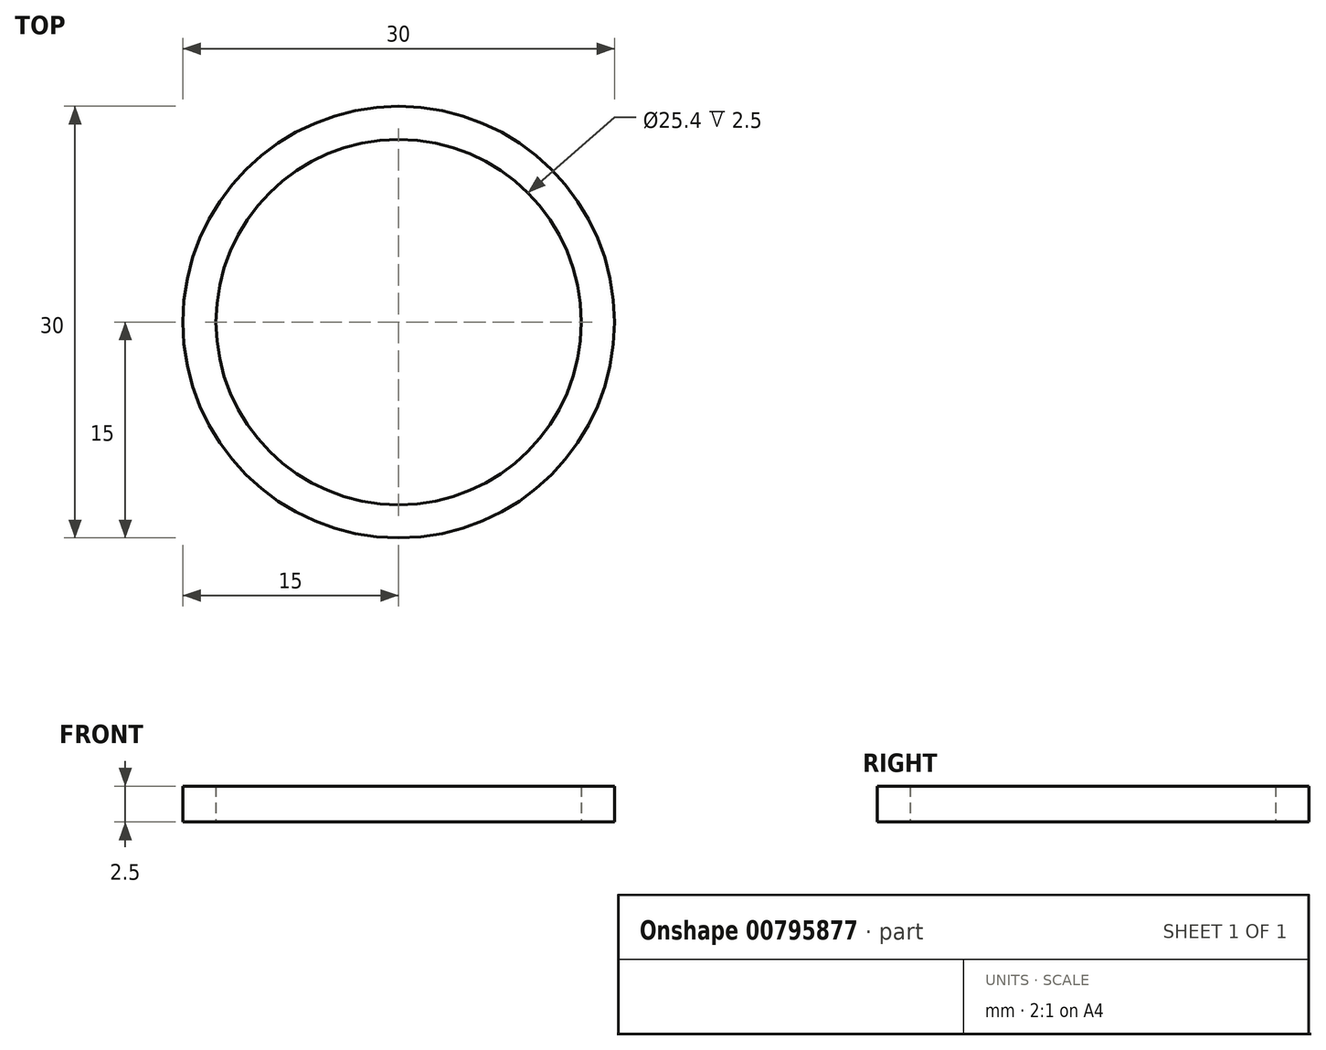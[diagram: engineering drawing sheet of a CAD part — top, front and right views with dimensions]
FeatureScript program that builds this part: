
annotation { "Feature Type Name" : "Feature", "Feature Type Description" : "" }
export const myFeature = defineFeature(function(context is Context, id is Id, definition is map)
    precondition{}
    {
        {
            var Q0;
            Q0=qCreatedBy(makeId("Top.planeOp"),FACE);
            var sketch = newSketch(context, id + "F0", { "sketchPlane" : qUnion([Q0])});
            skCircle(sketch, "E0", {"center": v(0, 0) * mm, "radius": 15 * mm});
            skCircle(sketch, "E1", {"center": v(0, 0) * mm, "radius": 12.7 * mm});
            skSolve(sketch);
        }
        {
            var Q0;
            Q0=makeQuery(id+"F0.imprint","IMPRINT",FACE,{"disambiguationData":[TD([[makeQuery(id+"F0.imprint","IMPRINT",EDGE,{"derivedFrom":sQuery(id+"F0.wireOp",EDGE,"E0")}),1.0]])]});
            extrude(context, id + "F1", {"entities" : qUnion([Q0]), "depth" : 2.5 * mm, "offsetDistance" : 25.4 * mm});
        }
    });
